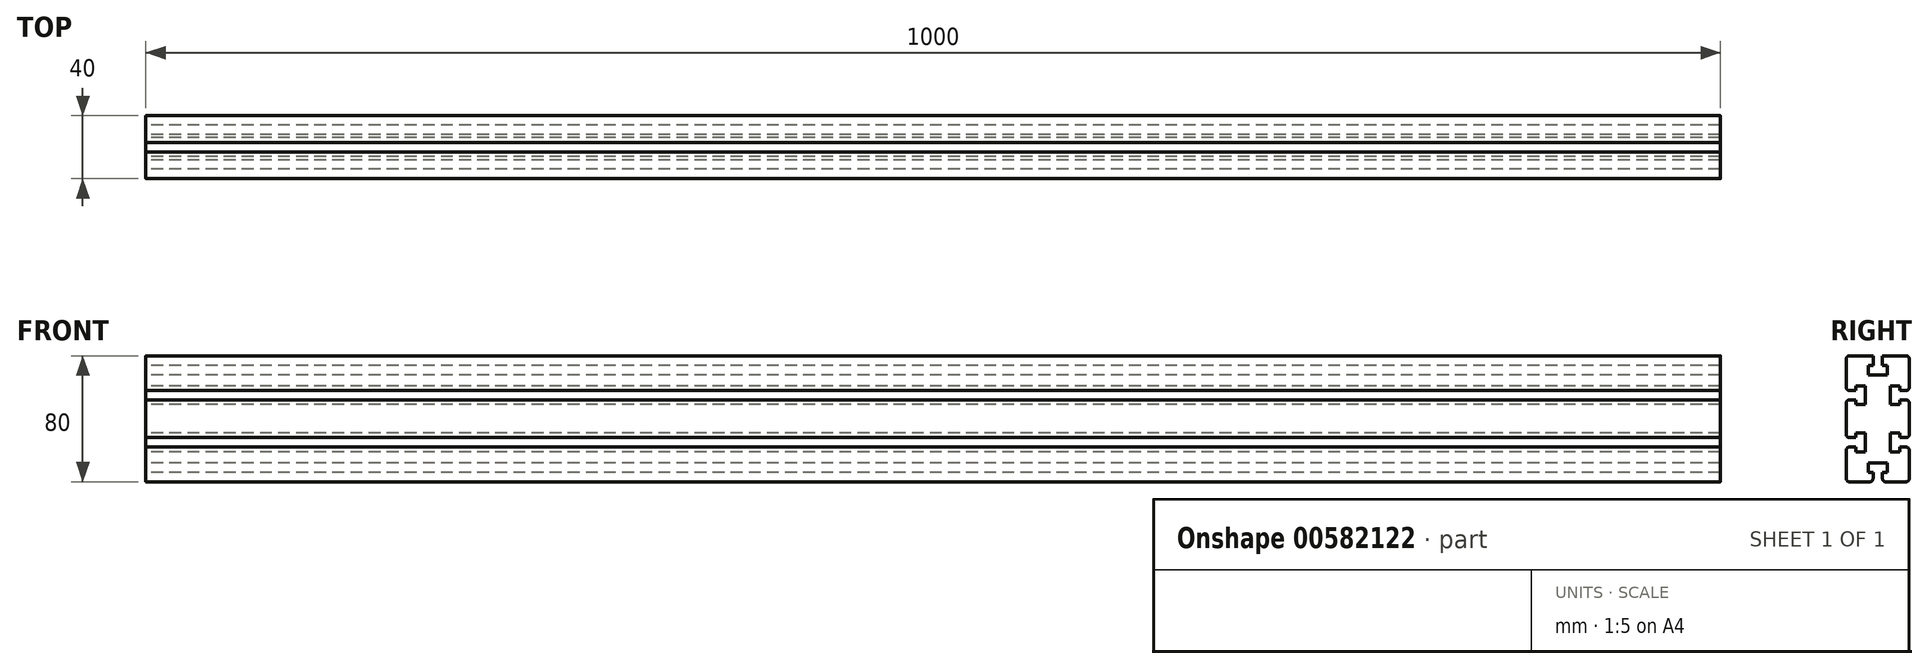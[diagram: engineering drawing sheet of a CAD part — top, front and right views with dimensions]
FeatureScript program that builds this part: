
annotation { "Feature Type Name" : "Feature", "Feature Type Description" : "" }
export const myFeature = defineFeature(function(context is Context, id is Id, definition is map)
    precondition{}
    {
        {
            var Q0;
            Q0=qCreatedBy(makeId("Right.planeOp"),FACE);
            var sketch = newSketch(context, id + "F0", { "sketchPlane" : qUnion([Q0])});
            skLineSegment(sketch, "E0.bottom", {"start": v(-20, 40) * mm, "end": v(-3, 40) * mm});
            skLineSegment(sketch, "E0.top", {"start": v(-20, -40) * mm, "end": v(-3, -40) * mm});
            skLineSegment(sketch, "E0.left", {"start": v(-20, 40) * mm, "end": v(-20, 18) * mm});
            skLineSegment(sketch, "E0.right", {"start": v(20, 40) * mm, "end": v(20, 18) * mm});
            skPoint(sketch, "E0.middle", {"position": v(0, 0) * mm});
            skLineSegment(sketch, "E1.left", {"start": v(-3, 34) * mm, "end": v(-3, 40) * mm});
            skLineSegment(sketch, "E1.right", {"start": v(3, 34) * mm, "end": v(3, 40) * mm});
            skPoint(sketch, "E1.middle", {"position": v(0, 40) * mm});
            skLineSegment(sketch, "E2.bottom", {"start": v(6, 34) * mm, "end": v(3, 34) * mm});
            skLineSegment(sketch, "E2.top", {"start": v(6, 28) * mm, "end": v(-6, 28) * mm});
            skLineSegment(sketch, "E2.left", {"start": v(6, 34) * mm, "end": v(6, 28) * mm});
            skLineSegment(sketch, "E2.right", {"start": v(-6, 34) * mm, "end": v(-6, 28) * mm});
            skPoint(sketch, "E2.middle", {"position": v(0, 31) * mm});
            skPoint(sketch, "E1.top.end.orphan", {"position": v(3, 46) * mm});
            skPoint(sketch, "E3.orphan", {"position": v(-3, 46) * mm});
            skLineSegment(sketch, "E4.trimOffspring", {"start": v(3, 40) * mm, "end": v(20, 40) * mm});
            skLineSegment(sketch, "E5.trimOffspring", {"start": v(-3, 34) * mm, "end": v(-6, 34) * mm});
            skPoint(sketch, "E6.middle", {"position": v(-20, 15) * mm});
            skPoint(sketch, "E7.middle", {"position": v(-11, 15) * mm});
            skLineSegment(sketch, "E8.bottom", {"start": v(-20, -18) * mm, "end": v(-14, -18) * mm});
            skLineSegment(sketch, "E8.top", {"start": v(-20, -12) * mm, "end": v(-14, -12) * mm});
            skPoint(sketch, "E8.middle", {"position": v(-20, -15) * mm});
            skLineSegment(sketch, "E9.bottom", {"start": v(-14, -9) * mm, "end": v(-8, -9) * mm});
            skLineSegment(sketch, "E9.top", {"start": v(-14, -21) * mm, "end": v(-8, -21) * mm});
            skLineSegment(sketch, "E9.left", {"start": v(-14, -9) * mm, "end": v(-14, -12) * mm});
            skLineSegment(sketch, "E9.right", {"start": v(-8, -9) * mm, "end": v(-8, -21) * mm});
            skPoint(sketch, "E9.middle", {"position": v(-11, -15) * mm});
            skPoint(sketch, "E6.left.end.orphan", {"position": v(-14.75, 18) * mm});
            skPoint(sketch, "E6.left.start.orphan", {"position": v(-14.75, 12) * mm});
            skPoint(sketch, "E6.right.end.orphan", {"position": v(-25.25, 18) * mm});
            skPoint(sketch, "E6.right.start.orphan", {"position": v(-25.25, 12) * mm});
            skPoint(sketch, "E7.bottom.start.orphan", {"position": v(-14, 21) * mm});
            skPoint(sketch, "E7.right.start.orphan", {"position": v(-8, 20.4) * mm});
            skPoint(sketch, "E7.top.end.orphan", {"position": v(-8, 9) * mm});
            skPoint(sketch, "E7.top.start.orphan", {"position": v(-14, 9.6) * mm});
            skLineSegment(sketch, "E10.bottom", {"start": v(-14, 18) * mm, "end": v(-20, 18) * mm});
            skLineSegment(sketch, "E10.top", {"start": v(-14, 12) * mm, "end": v(-20, 12) * mm});
            skLineSegment(sketch, "E11.bottom", {"start": v(-14, 21) * mm, "end": v(-8, 21) * mm});
            skLineSegment(sketch, "E11.top", {"start": v(-14, 9) * mm, "end": v(-8, 9) * mm});
            skLineSegment(sketch, "E11.right", {"start": v(-8, 21) * mm, "end": v(-8, 9) * mm});
            skLineSegment(sketch, "E12.bottom", {"start": v(14, 12) * mm, "end": v(20, 12) * mm});
            skLineSegment(sketch, "E12.top", {"start": v(14, 18) * mm, "end": v(20, 18) * mm});
            skPoint(sketch, "E12.middle", {"position": v(20, 15) * mm});
            skLineSegment(sketch, "E13.bottom", {"start": v(14, 21) * mm, "end": v(8, 21) * mm});
            skLineSegment(sketch, "E13.top", {"start": v(14, 9) * mm, "end": v(8, 9) * mm});
            skLineSegment(sketch, "E13.left", {"start": v(14, 21) * mm, "end": v(14, 18) * mm});
            skLineSegment(sketch, "E13.right", {"start": v(8, 21) * mm, "end": v(8, 9) * mm});
            skPoint(sketch, "E13.middle", {"position": v(11, 15) * mm});
            skPoint(sketch, "E13.middle.positionSnap0", {"position": v(14, 15) * mm});
            skPoint(sketch, "E13.centerSnap0", {"position": v(14, 15) * mm});
            skLineSegment(sketch, "E14.bottom", {"start": v(14, -18) * mm, "end": v(20, -18) * mm});
            skLineSegment(sketch, "E14.top", {"start": v(14, -12) * mm, "end": v(20, -12) * mm});
            skPoint(sketch, "E14.middle", {"position": v(20, -15) * mm});
            skLineSegment(sketch, "E15.bottom", {"start": v(14, -9) * mm, "end": v(8, -9) * mm});
            skLineSegment(sketch, "E15.top", {"start": v(14, -21) * mm, "end": v(8, -21) * mm});
            skLineSegment(sketch, "E15.left", {"start": v(14, -9) * mm, "end": v(14, -12) * mm});
            skLineSegment(sketch, "E15.right", {"start": v(8, -9) * mm, "end": v(8, -21) * mm});
            skPoint(sketch, "E15.middle", {"position": v(11, -15) * mm});
            skPoint(sketch, "E15.middle.positionSnap0", {"position": v(14, -15) * mm});
            skPoint(sketch, "E15.centerSnap0", {"position": v(14, -15) * mm});
            skLineSegment(sketch, "E16.left", {"start": v(-3, -34) * mm, "end": v(-3, -40) * mm});
            skLineSegment(sketch, "E16.right", {"start": v(3, -34) * mm, "end": v(3, -40) * mm});
            skPoint(sketch, "E16.middle", {"position": v(0, -40) * mm});
            skLineSegment(sketch, "E17.bottom", {"start": v(6, -34) * mm, "end": v(3, -34) * mm});
            skLineSegment(sketch, "E17.top", {"start": v(6, -28) * mm, "end": v(-6, -28) * mm});
            skLineSegment(sketch, "E17.left", {"start": v(6, -34) * mm, "end": v(6, -28) * mm});
            skLineSegment(sketch, "E17.right", {"start": v(-6, -34) * mm, "end": v(-6, -28) * mm});
            skPoint(sketch, "E17.middle", {"position": v(0, -31) * mm});
            skPoint(sketch, "E17.middle.positionSnap0", {"position": v(0, -34) * mm});
            skPoint(sketch, "E17.centerSnap0", {"position": v(0, -34) * mm});
            skPoint(sketch, "E18.orphan", {"position": v(-28.22, 18) * mm});
            skPoint(sketch, "E19.orphan", {"position": v(-28.22, 12) * mm});
            skLineSegment(sketch, "E20.trimOffspring", {"start": v(-20, 12) * mm, "end": v(-20, -12) * mm});
            skLineSegment(sketch, "E21.trimOffspring", {"start": v(-14, 12) * mm, "end": v(-14, 9) * mm});
            skPoint(sketch, "E22.orphan", {"position": v(-11.78, 18) * mm});
            skPoint(sketch, "E23.orphan", {"position": v(-11.78, 12) * mm});
            skLineSegment(sketch, "E24", {"start": v(-14, 21) * mm, "end": v(-14, 18) * mm});
            skLineSegment(sketch, "E25.trimOffspring", {"start": v(14, 12) * mm, "end": v(14, 9) * mm});
            skPoint(sketch, "E26.orphan", {"position": v(26, 18) * mm});
            skPoint(sketch, "E27.orphan", {"position": v(26, 12) * mm});
            skLineSegment(sketch, "E28.trimOffspring", {"start": v(20, 12) * mm, "end": v(20, -12) * mm});
            skPoint(sketch, "E14.right.end.orphan", {"position": v(26, -12) * mm});
            skPoint(sketch, "E14.right.start.orphan", {"position": v(26, -18) * mm});
            skLineSegment(sketch, "E29.trimOffspring", {"start": v(20, -18) * mm, "end": v(20, -40) * mm});
            skLineSegment(sketch, "E30.trimOffspring", {"start": v(14, -18) * mm, "end": v(14, -21) * mm});
            skLineSegment(sketch, "E31.trimOffspring", {"start": v(-14, -18) * mm, "end": v(-14, -21) * mm});
            skPoint(sketch, "E32.orphan", {"position": v(-26, -12) * mm});
            skPoint(sketch, "E33.orphan", {"position": v(-26, -18) * mm});
            skLineSegment(sketch, "E34.trimOffspring", {"start": v(-20, -18) * mm, "end": v(-20, -40) * mm});
            skLineSegment(sketch, "E35.trimOffspring", {"start": v(-3, -34) * mm, "end": v(-6, -34) * mm});
            skLineSegment(sketch, "E36.trimOffspring", {"start": v(3, -40) * mm, "end": v(20, -40) * mm});
            skPoint(sketch, "E16.top.end.orphan", {"position": v(3, -46) * mm});
            skPoint(sketch, "E37.orphan", {"position": v(-3, -46) * mm});
            skSolve(sketch);
        }
        {
            var Q0;
            Q0 = qSketchRegion(id + "F0", true);
            extrude(context, id + "F1", {"entities" : qUnion([Q0]), "depth" : 1000 * mm, "offsetDistance" : 25 * mm});
        }
        {
            var Q0;
            Q0=makeQuery(id+"F1.opExtrude","SWEPT_EDGE",EDGE,{"disambiguationData":[OSD([sQuery(id+"F0.wireOp",EDGE,"E0.bottom"),sQuery(id+"F0.wireOp",EDGE,"E0.left")])]});
            var Q1;
            Q1=makeQuery(id+"F1.opExtrude","SWEPT_EDGE",EDGE,{"disambiguationData":[OSD([sQuery(id+"F0.wireOp",EDGE,"E0.left"),sQuery(id+"F0.wireOp",EDGE,"E10.bottom")])]});
            var Q2;
            Q2=makeQuery(id+"F1.opExtrude","SWEPT_EDGE",EDGE,{"disambiguationData":[OSD([sQuery(id+"F0.wireOp",EDGE,"E10.top"),sQuery(id+"F0.wireOp",EDGE,"E20.trimOffspring")])]});
            var Q3;
            Q3=makeQuery(id+"F1.opExtrude","SWEPT_EDGE",EDGE,{"disambiguationData":[OSD([sQuery(id+"F0.wireOp",EDGE,"E8.top"),sQuery(id+"F0.wireOp",EDGE,"E20.trimOffspring")])]});
            var Q4;
            Q4=makeQuery(id+"F1.opExtrude","SWEPT_EDGE",EDGE,{"disambiguationData":[OSD([sQuery(id+"F0.wireOp",EDGE,"E8.bottom"),sQuery(id+"F0.wireOp",EDGE,"E34.trimOffspring")])]});
            var Q5;
            Q5=makeQuery(id+"F1.opExtrude","SWEPT_EDGE",EDGE,{"disambiguationData":[OSD([sQuery(id+"F0.wireOp",EDGE,"E0.top"),sQuery(id+"F0.wireOp",EDGE,"E34.trimOffspring")])]});
            var Q6;
            Q6=makeQuery(id+"F1.opExtrude","SWEPT_EDGE",EDGE,{"disambiguationData":[OSD([sQuery(id+"F0.wireOp",EDGE,"E0.top"),sQuery(id+"F0.wireOp",EDGE,"E16.left")])]});
            var Q7;
            Q7=makeQuery(id+"F1.opExtrude","SWEPT_EDGE",EDGE,{"disambiguationData":[OSD([sQuery(id+"F0.wireOp",EDGE,"E16.right"),sQuery(id+"F0.wireOp",EDGE,"E36.trimOffspring")])]});
            var Q8;
            Q8=makeQuery(id+"F1.opExtrude","SWEPT_EDGE",EDGE,{"disambiguationData":[OSD([sQuery(id+"F0.wireOp",EDGE,"E29.trimOffspring"),sQuery(id+"F0.wireOp",EDGE,"E36.trimOffspring")])]});
            var Q9;
            Q9=makeQuery(id+"F1.opExtrude","SWEPT_EDGE",EDGE,{"disambiguationData":[OSD([sQuery(id+"F0.wireOp",EDGE,"E14.bottom"),sQuery(id+"F0.wireOp",EDGE,"E29.trimOffspring")])]});
            var Q10;
            Q10=makeQuery(id+"F1.opExtrude","SWEPT_EDGE",EDGE,{"disambiguationData":[OSD([sQuery(id+"F0.wireOp",EDGE,"E12.bottom"),sQuery(id+"F0.wireOp",EDGE,"E28.trimOffspring")])]});
            var Q11;
            Q11=makeQuery(id+"F1.opExtrude","SWEPT_EDGE",EDGE,{"disambiguationData":[OSD([sQuery(id+"F0.wireOp",EDGE,"E14.top"),sQuery(id+"F0.wireOp",EDGE,"E28.trimOffspring")])]});
            var Q12;
            Q12=makeQuery(id+"F1.opExtrude","SWEPT_EDGE",EDGE,{"disambiguationData":[OSD([sQuery(id+"F0.wireOp",EDGE,"E0.right"),sQuery(id+"F0.wireOp",EDGE,"E4.trimOffspring")])]});
            var Q13;
            Q13=makeQuery(id+"F1.opExtrude","SWEPT_EDGE",EDGE,{"disambiguationData":[OSD([sQuery(id+"F0.wireOp",EDGE,"E0.right"),sQuery(id+"F0.wireOp",EDGE,"E12.top")])]});
            fillet(context, id + "F2", {"entities" : qUnion([Q0, Q1, Q2, Q3, Q4, Q5, Q6, Q7, Q8, Q9, Q10, Q11, Q12, Q13]), "radius" : 2 * mm, "tangentPropagation" : true, "allowEdgeOverflow" : false});
        }
    });
